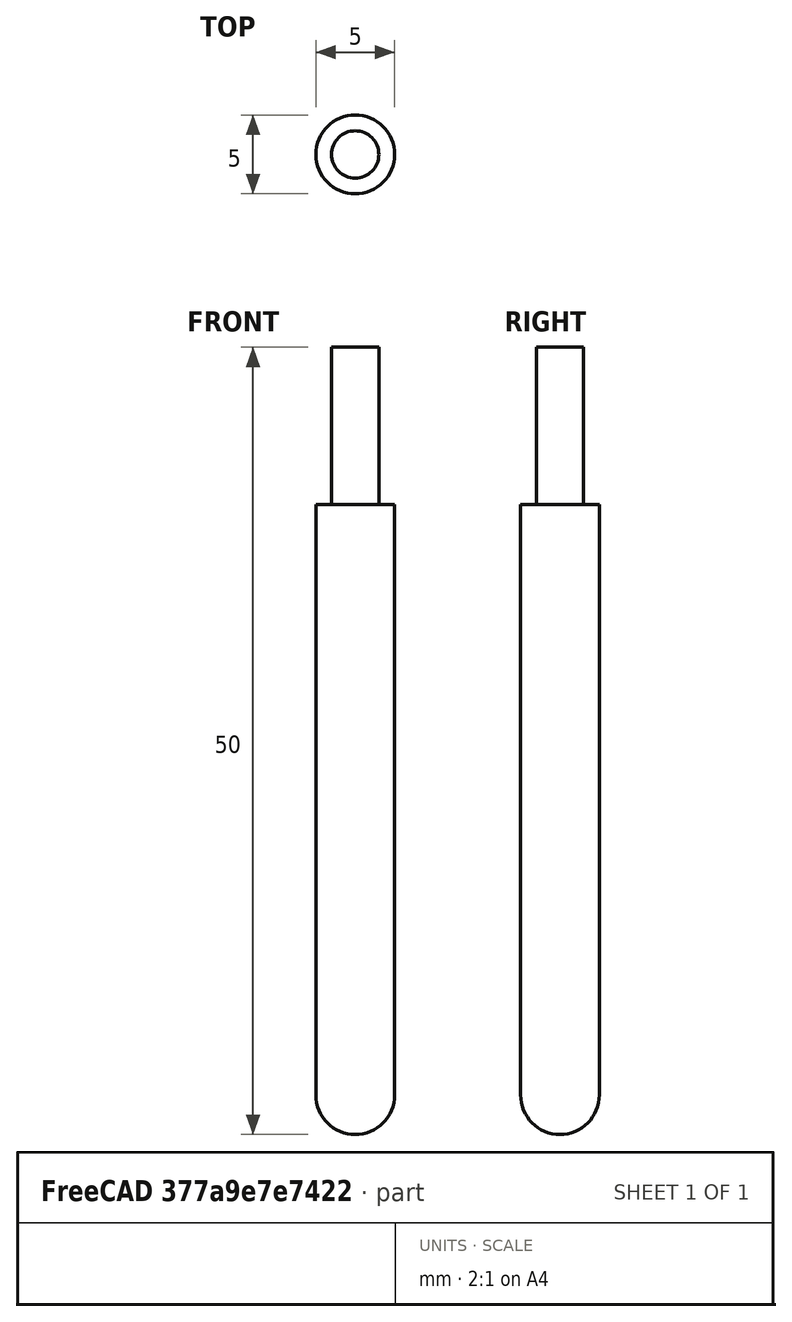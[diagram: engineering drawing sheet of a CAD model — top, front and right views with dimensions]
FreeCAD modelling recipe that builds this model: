
FCSTD DOCUMENT  (FreeCAD 1.0R39109 (Git))
Label: ballend
License: Creative Commons Attribution 4.0
LicenseURL: https://creativecommons.org/licenses/by/4.0/
objects: Sketcher::SketchObject×1, PartDesign::Revolution×1, App::FeaturePython×1, PartDesign::Body×1
note: 6 computed .brp shape members not serialized (recipe doc carries the construction recipe); baked Part::Feature solids carry a one-line shape summary decoded from their .brp

FEATURE [Sketcher::SketchObject] Sketch
  ArcFitTolerance = 0
  AttachmentSupport = -> [XZ_Plane]
  FullyConstrained = true
  MakeInternals = false
  MapMode = 5
  Placement = pos=(0,0,0) rot=(1,0,0;1.5708rad)
  expr: Constraints[10] = <<Attributes>>.ShankDiameter
  expr: Constraints[17] = <<Attributes>>.CuttingEdgeHeight
  expr: Constraints[3] = <<Attributes>>.Diameter
  expr: Constraints[4] = <<Attributes>>.Length
  sketch-geometry (8):
    g0: LineSegment StartX=-9e-16 StartY=50 StartZ=0 EndX=-9e-16 EndY=0 EndZ=0
    g1: LineSegment StartX=2.5 StartY=2.5 StartZ=0 EndX=2.5 EndY=40 EndZ=0
    g2: LineSegment StartX=1.5 StartY=50 StartZ=0 EndX=-9e-16 EndY=50 EndZ=0
    g3: LineSegment [constr] StartX=2.5 StartY=0 StartZ=0 EndX=-2.5 EndY=0 EndZ=0
    g4: LineSegment StartX=1.5 StartY=40.01 StartZ=0 EndX=2.5 EndY=40 EndZ=0
    g5: LineSegment StartX=1.5 StartY=50 StartZ=0 EndX=1.5 EndY=40.01 EndZ=0
    g6: LineSegment [constr] StartX=-1.5 StartY=50 StartZ=0 EndX=1.5 EndY=50 EndZ=0
    g7: ArcOfCircle CenterX=-5e-16 CenterY=2.5 CenterZ=0 NormalX=0 NormalY=0 NormalZ=1 AngleXU=0 Radius=2.5 StartAngle=4.71239 EndAngle=6.28319
  constraints (21):
    c: Vertical(g0)
    c: Vertical(g1)
    c: Horizontal(g2)
    c: DistanceX(g3,g3) = 5
    c: DistanceY(g3,g2) = 50
    c: Coincident(g1,g4)
    c: Vertical(g5)
    c: Coincident(g2,g5)
    c: Symmetric(g6,g6,g0)
    c: Coincident(g6,g2)
    c: DistanceX(g6,g6) = 3
    c: Coincident(g4,g5)
    c: Tangent(g1,g7) = -1.5708
    c: PointOnObject(g0,g3)
    c: Symmetric(g3,g3,g-2)
    c: Vertical(g3,g1)
    c: Perpendicular(g7,g0) = 4.71239
    c: DistanceY(g0,g1) = 40
    c: Coincident(g2,g0)
    c: Coincident(g0,g-1)
    c: DistanceY(g1,g4) = 0.01
FEATURE [PartDesign::Revolution] Revolution
  AllowMultiFace = false
  Angle = 360
  Angle2 = 60
  Axis = (0,2e-16,1)
  Base = (0,0,0)
  Placement = pos=(0,0,0) rot=(1,0,0;1.5708rad)
  Profile = -> Sketch
  ReferenceAxis = -> Sketch [V_Axis]
  Reversed = true
  Suppressed = false
  Type = 0
FEATURE [App::FeaturePython] PropertyBag  label="Attributes"  # WARN: FeaturePython — macro-defined, semantics opaque (R4)
  CustomPropertyGroups = 0
  CuttingEdgeHeight = 40
  Diameter = 5
  Flutes = 2
  Length = 50
  ShankDiameter = 3
FEATURE [PartDesign::Body] Body  label="Ballend"
  AllowCompound = false
  Group = -> [Sketch,Revolution,PropertyBag]
  Origin = -> Origin
  Tip = -> Revolution
